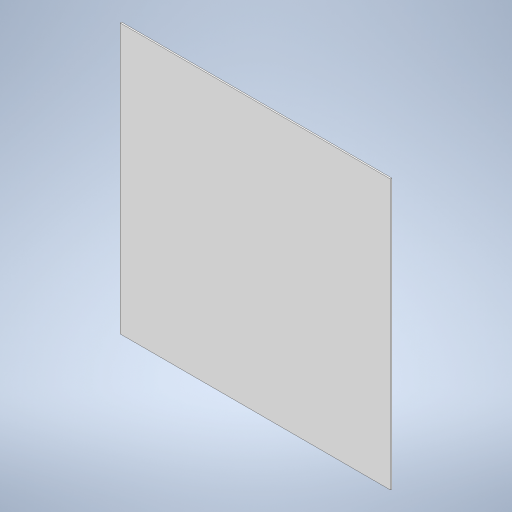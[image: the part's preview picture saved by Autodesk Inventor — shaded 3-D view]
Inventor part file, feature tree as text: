
AUTODESK INVENTOR PART (.ipt)
format: ipt  version: 2023 (Build 270158000, 158)  size: 194,560 bytes
history: native  units: mm
features: extrude x1, sketch x1
ambient origin geometry x8: Origin, YZ Plane, XZ Plane, XY Plane, X Axis, Y Axis, Z Axis, Center Point
bodies: Solid1 (feature_tree)
feature tree (2):
  extrude  "Extrusion1"  Depth=540.0mm
  sketch  "Sketch1"  dims[d0=542.0mm d1=540.0mm d2=3.0mm d3=0.0mm]
